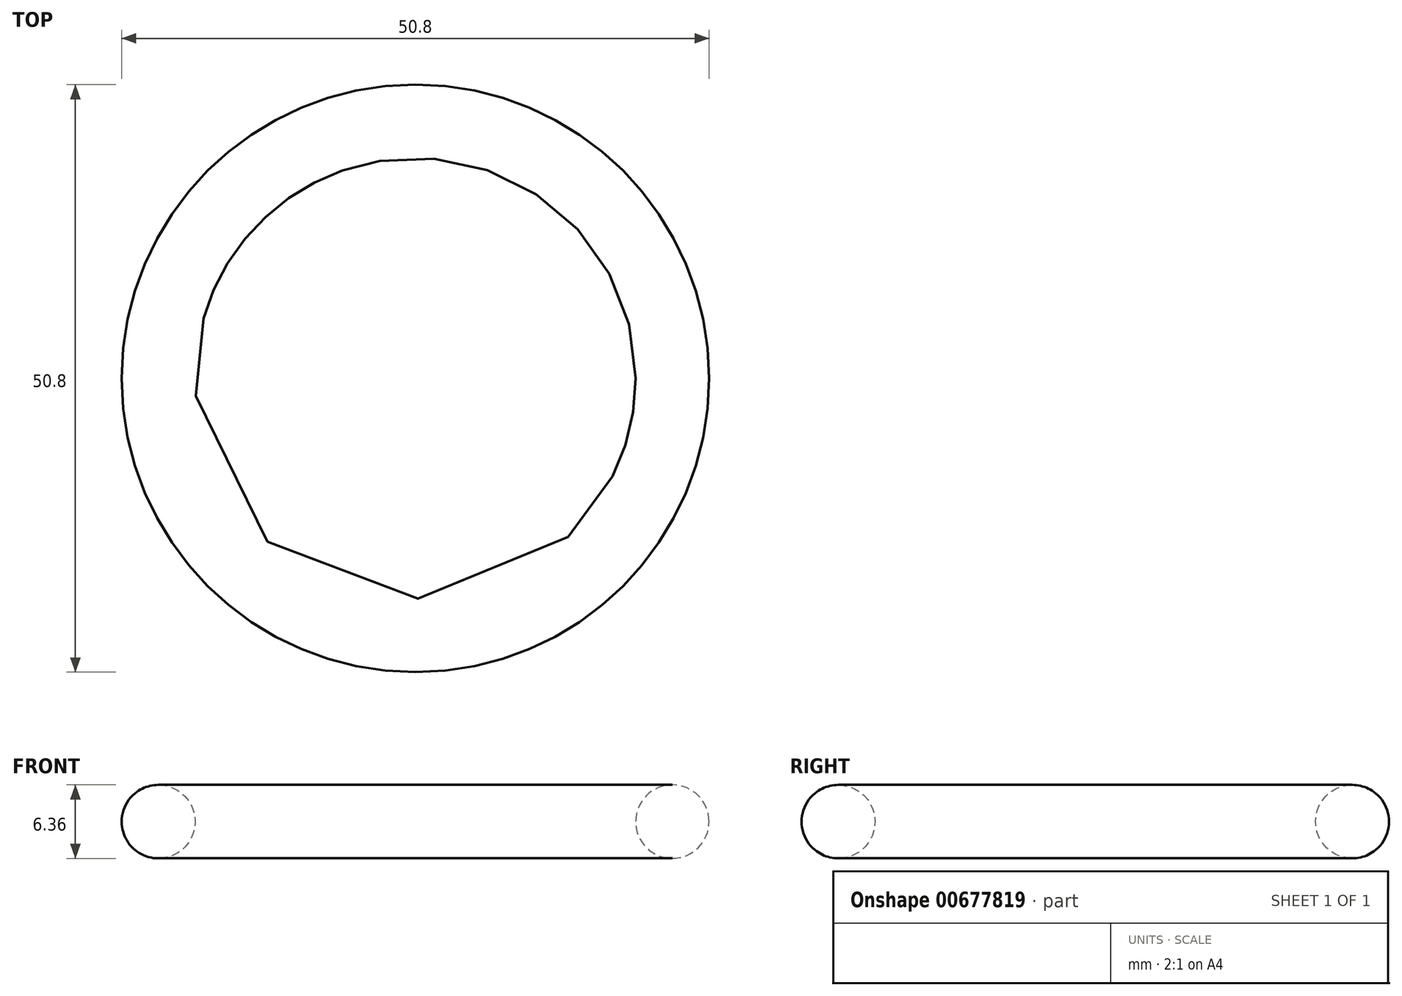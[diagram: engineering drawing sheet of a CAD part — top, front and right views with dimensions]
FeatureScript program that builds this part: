
annotation { "Feature Type Name" : "Feature", "Feature Type Description" : "" }
export const myFeature = defineFeature(function(context is Context, id is Id, definition is map)
    precondition{}
    {
        {
            var Q0;
            Q0=qCreatedBy(makeId("Front.planeOp"),FACE);
            var sketch = newSketch(context, id + "F0", { "sketchPlane" : qUnion([Q0])});
            skCircle(sketch, "E0", {"center": v(-22.23, 0) * mm, "radius": 3.18 * mm});
            skLineSegment(sketch, "E1", {"start": v(0, 8.14) * mm, "end": v(0, -10.41) * mm, "construction": true});
            skSolve(sketch);
        }
        {
            var Q0;
            Q0 = qSketchRegion(id + "F0", true);
            var Q1;
            Q1=sQuery(id+"F0.wireOp",EDGE,"E1");
            revolve(context, id + "F1", {"entities" : qUnion([Q0]), "axis" : qUnion([Q1]), "revolveType" : RevolveType.FULL});
        }
    });
